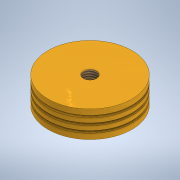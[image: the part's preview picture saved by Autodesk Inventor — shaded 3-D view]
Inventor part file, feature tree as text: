
AUTODESK INVENTOR PART (.ipt)
format: ipt  version: 2020 (Build 240168000, 168)  size: 161,792 bytes
history: native  units: mm
features: sketch x8, extrude x7, hole x1, thread x1
ambient origin geometry x8: Origin, YZ Plane, XZ Plane, XY Plane, X Axis, Y Axis, Z Axis, Center Point
bodies: Solid1 (feature_tree)
feature tree (17):
  extrude  "Extrusion1"  Depth=1.25mm TaperAngle=0.0deg
  extrude  "Extrusion2"  Depth=0.5mm TaperAngle=0.0deg
  extrude  "Extrusion3"  Depth=1.0mm TaperAngle=0.0deg
  extrude  "Extrusion4"  Depth=0.5mm TaperAngle=0.0deg
  extrude  "Extrusion5"  Depth=1.0mm TaperAngle=0.0deg
  extrude  "Extrusion6"  Depth=0.5mm TaperAngle=0.0deg
  extrude  "Extrusion7"  Depth=1.25mm TaperAngle=0.0deg
  hole  "Hole1"  [1 undecoded]
  thread  "Thread1"  [1 undecoded]
  sketch  "Sketch1"  dims[d0=19.0mm d1=1.25mm d2=0.0mm]
  sketch  "Sketch2"  dims[d3=16.0mm d4=0.5mm d5=0.0mm]
  sketch  "Sketch3"  dims[d6=19.0mm d7=1.0mm d8=0.0mm]
  sketch  "Sketch4"  dims[d9=16.0mm d10=0.5mm d11=0.0mm]
  sketch  "Sketch5"  dims[d12=19.0mm d13=1.0mm d14=0.0mm]
  sketch  "Sketch6"  dims[d15=16.0mm d16=0.5mm d17=0.0mm]
  sketch  "Sketch7"  dims[d18=19.0mm d19=1.25mm d20=0.0mm]
  sketch  "Sketch8"  dims[d21=3.0mm d22=3.0mm d23=6.0mm d24=4.0mm d25=2.0mm d26=90.0deg d27=3.5mm d28=20.594885mm d29=6.25mm d30=0.0mm]
note: 2 required parameter values undecoded (feature->parameter linkage not recoverable at this tier; creation-order binding heuristic only, values carry confidence <= 0.55)
